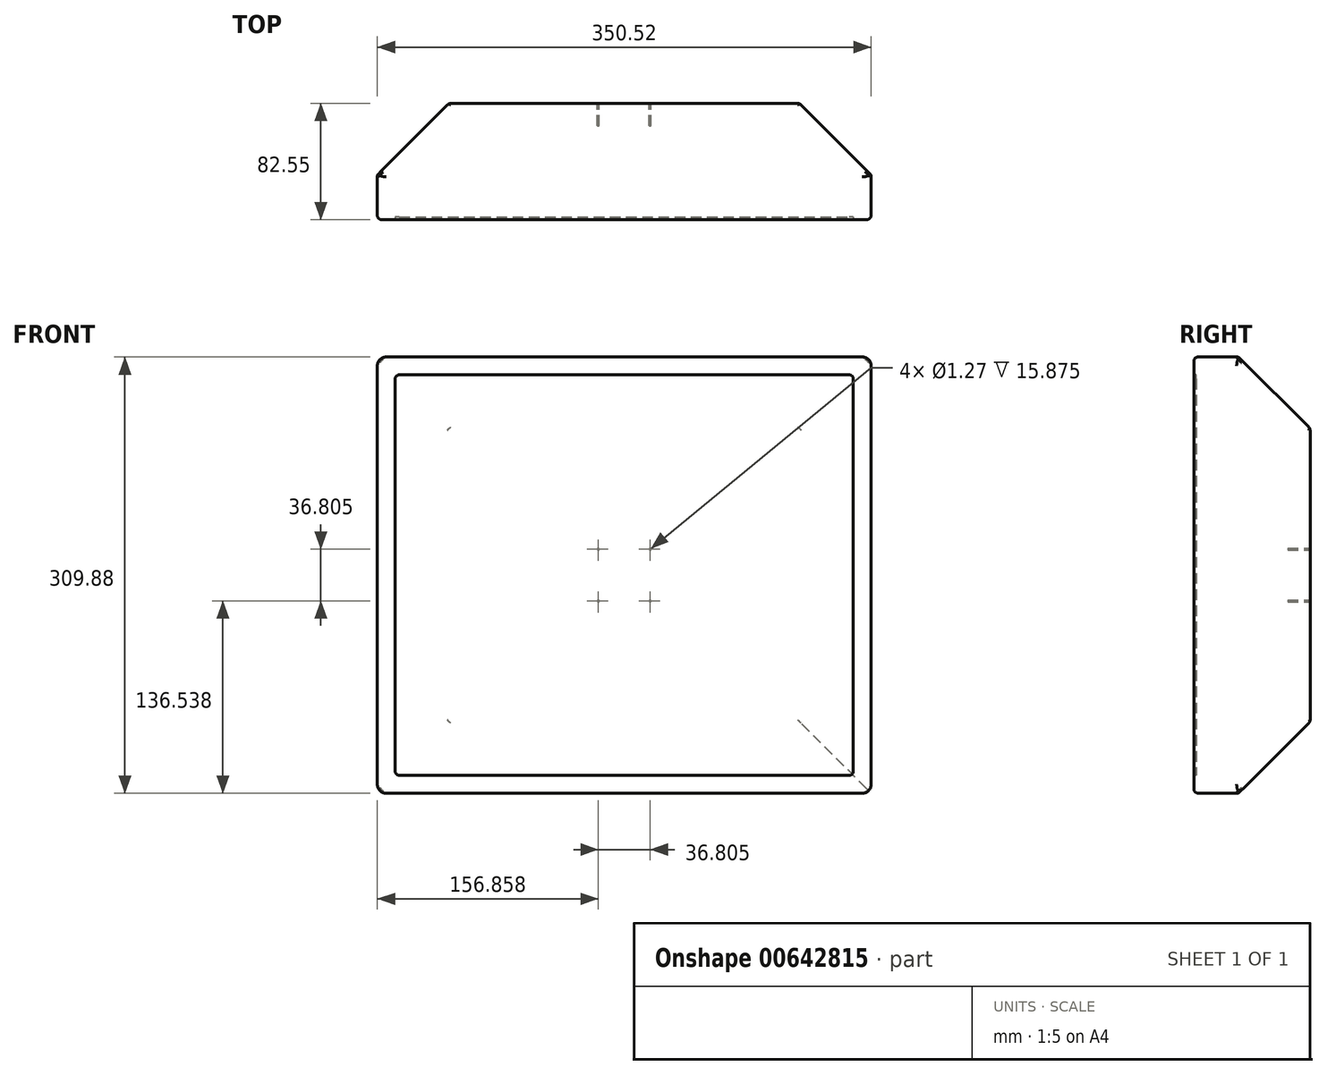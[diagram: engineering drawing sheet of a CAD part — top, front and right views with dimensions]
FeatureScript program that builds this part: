
annotation { "Feature Type Name" : "Feature", "Feature Type Description" : "" }
export const myFeature = defineFeature(function(context is Context, id is Id, definition is map)
    precondition{}
    {
        {
            var Q0;
            Q0=qCreatedBy(makeId("Front.planeOp"),FACE);
            var sketch = newSketch(context, id + "F0", { "sketchPlane" : qUnion([Q0])});
            skLineSegment(sketch, "E0.bottom", {"start": v(175.26, 154.94) * mm, "end": v(-175.26, 154.94) * mm});
            skLineSegment(sketch, "E0.top", {"start": v(175.26, -154.94) * mm, "end": v(-175.26, -154.94) * mm});
            skLineSegment(sketch, "E0.left", {"start": v(175.26, 154.94) * mm, "end": v(175.26, -154.94) * mm});
            skLineSegment(sketch, "E0.right", {"start": v(-175.26, 154.94) * mm, "end": v(-175.26, -154.94) * mm});
            skPoint(sketch, "E0.middle", {"position": v(0, 0) * mm});
            skSolve(sketch);
        }
        {
            var Q0;
            Q0 = qSketchRegion(id + "F0", true);
            extrude(context, id + "F1", {"entities" : qUnion([Q0]), "oppositeDirection" : true, "depth" : 25.4 * mm, "offsetDistance" : 25.4 * mm});
        }
        {
            var Q0;
            Q0=makeQuery(id+"F1.opExtrude","CAP_FACE",FACE,{"disambiguationData":[OSD([sQuery(id+"F0.wireOp",EDGE,"E0.bottom"),sQuery(id+"F0.wireOp",EDGE,"E0.top"),sQuery(id+"F0.wireOp",EDGE,"E0.left"),sQuery(id+"F0.wireOp",EDGE,"E0.right")])],"isStart":false});
            var sketch = newSketch(context, id + "F2", { "sketchPlane" : qUnion([Q0])});
            skLineSegment(sketch, "E1.bottom", {"start": v(175.26, 154.94) * mm, "end": v(-175.26, 154.94) * mm});
            skLineSegment(sketch, "E1.top", {"start": v(175.26, -154.94) * mm, "end": v(-175.26, -154.94) * mm});
            skLineSegment(sketch, "E1.left", {"start": v(175.26, 154.94) * mm, "end": v(175.26, -154.94) * mm});
            skLineSegment(sketch, "E1.right", {"start": v(-175.26, 154.94) * mm, "end": v(-175.26, -154.94) * mm});
            skSolve(sketch);
        }
        {
            var Q0;
            Q0 = qSketchRegion(id + "F2", true);
            extrude(context, id + "F3", {"entities" : qUnion([Q0]), "operationType" : NewBodyOperationType.ADD, "depth" : 57.15 * mm, "offsetDistance" : 25.4 * mm});
        }
        {
            var Q0;
            Q0=makeQuery(id+"F3.opExtrude","CAP_EDGE",EDGE,{"disambiguationData":[OSD([sQuery(id+"F2.wireOp",EDGE,"E1.bottom")])],"isStart":false});
            var Q1;
            Q1=makeQuery(id+"F3.opExtrude","CAP_EDGE",EDGE,{"disambiguationData":[OSD([sQuery(id+"F2.wireOp",EDGE,"E1.right")])],"isStart":false});
            var Q2;
            Q2=makeQuery(id+"F3.opExtrude","CAP_EDGE",EDGE,{"disambiguationData":[OSD([sQuery(id+"F2.wireOp",EDGE,"E1.top")])],"isStart":false});
            var Q3;
            Q3=makeQuery(id+"F3.opExtrude","CAP_EDGE",EDGE,{"disambiguationData":[OSD([sQuery(id+"F2.wireOp",EDGE,"E1.left")])],"isStart":false});
            chamfer(context, id + "F4", {"entities" : qUnion([Q0, Q1, Q2, Q3]), "chamferType" : ChamferType.TWO_OFFSETS, "width1" : 50.8 * mm, "oppositeDirection" : false, "width2" : 50.8 * mm, "tangentPropagation" : true});
        }
        {
            var Q0;
            Q0=makeQuery(id+"F1.opExtrude","CAP_FACE",FACE,{"disambiguationData":[OSD([sQuery(id+"F0.wireOp",EDGE,"E0.bottom"),sQuery(id+"F0.wireOp",EDGE,"E0.top"),sQuery(id+"F0.wireOp",EDGE,"E0.left"),sQuery(id+"F0.wireOp",EDGE,"E0.right")])],"isStart":true});
            var sketch = newSketch(context, id + "F5", { "sketchPlane" : qUnion([Q0])});
            skLineSegment(sketch, "E2.bottom", {"start": v(-162.56, 142.24) * mm, "end": v(162.56, 142.24) * mm});
            skLineSegment(sketch, "E2.top", {"start": v(-162.56, -142.24) * mm, "end": v(162.56, -142.24) * mm});
            skLineSegment(sketch, "E2.left", {"start": v(-162.56, 142.24) * mm, "end": v(-162.56, -142.24) * mm});
            skLineSegment(sketch, "E2.right", {"start": v(162.56, 142.24) * mm, "end": v(162.56, -142.24) * mm});
            skSolve(sketch);
        }
        {
            var Q0;
            Q0 = qSketchRegion(id + "F5", true);
            extrude(context, id + "F6", {"entities" : qUnion([Q0]), "operationType" : NewBodyOperationType.REMOVE, "oppositeDirection" : true, "depth" : 1.9 * mm, "offsetDistance" : 25.4 * mm});
        }
        {
            var Q0;
            Q0=makeQuery(id+"F6.boolean.opBoolean","COPY",EDGE,{"derivedFrom":makeQuery(id+"F6.opExtrude","SWEPT_EDGE",EDGE,{"disambiguationData":[OSD([sQuery(id+"F5.wireOp",EDGE,"E2.bottom"),sQuery(id+"F5.wireOp",EDGE,"E2.left")])]})});
            var Q1;
            Q1=makeQuery(id+"F6.boolean.opBoolean","COPY",EDGE,{"derivedFrom":makeQuery(id+"F6.opExtrude","SWEPT_EDGE",EDGE,{"disambiguationData":[OSD([sQuery(id+"F5.wireOp",EDGE,"E2.top"),sQuery(id+"F5.wireOp",EDGE,"E2.left")])]})});
            var Q2;
            Q2=makeQuery(id+"F6.boolean.opBoolean","COPY",EDGE,{"derivedFrom":makeQuery(id+"F6.opExtrude","SWEPT_EDGE",EDGE,{"disambiguationData":[OSD([sQuery(id+"F5.wireOp",EDGE,"E2.top"),sQuery(id+"F5.wireOp",EDGE,"E2.right")])]})});
            var Q3;
            Q3=makeQuery(id+"F6.boolean.opBoolean","COPY",EDGE,{"derivedFrom":makeQuery(id+"F6.opExtrude","SWEPT_EDGE",EDGE,{"disambiguationData":[OSD([sQuery(id+"F5.wireOp",EDGE,"E2.bottom"),sQuery(id+"F5.wireOp",EDGE,"E2.right")])]})});
            fillet(context, id + "F7", {"entities" : qUnion([Q0, Q1, Q2, Q3]), "radius" : 2.87 * mm, "tangentPropagation" : true, "allowEdgeOverflow" : false});
        }
        {
            var Q0;
            Q0=makeQuery(id+"F3.boolean.opBoolean","MERGE",EDGE,{"derivedFrom":[makeQuery(id+"F1.opExtrude","SWEPT_EDGE",EDGE,{"disambiguationData":[OSD([sQuery(id+"F0.wireOp",EDGE,"E0.bottom"),sQuery(id+"F0.wireOp",EDGE,"E0.left")])]}),makeQuery(id+"F3.opExtrude","SWEPT_EDGE",EDGE,{"disambiguationData":[OSD([sQuery(id+"F2.wireOp",EDGE,"E1.bottom"),sQuery(id+"F2.wireOp",EDGE,"E1.right")])]})]});
            var Q1;
            Q1=makeQuery(id+"F3.boolean.opBoolean","MERGE",EDGE,{"derivedFrom":[makeQuery(id+"F1.opExtrude","SWEPT_EDGE",EDGE,{"disambiguationData":[OSD([sQuery(id+"F0.wireOp",EDGE,"E0.bottom"),sQuery(id+"F0.wireOp",EDGE,"E0.right")])]}),makeQuery(id+"F3.opExtrude","SWEPT_EDGE",EDGE,{"disambiguationData":[OSD([sQuery(id+"F2.wireOp",EDGE,"E1.bottom"),sQuery(id+"F2.wireOp",EDGE,"E1.left")])]})]});
            var Q2;
            Q2=makeQuery(id+"F3.boolean.opBoolean","MERGE",EDGE,{"derivedFrom":[makeQuery(id+"F1.opExtrude","SWEPT_EDGE",EDGE,{"disambiguationData":[OSD([sQuery(id+"F0.wireOp",EDGE,"E0.top"),sQuery(id+"F0.wireOp",EDGE,"E0.left")])]}),makeQuery(id+"F3.opExtrude","SWEPT_EDGE",EDGE,{"disambiguationData":[OSD([sQuery(id+"F2.wireOp",EDGE,"E1.top"),sQuery(id+"F2.wireOp",EDGE,"E1.right")])]})]});
            var Q3;
            Q3=makeQuery(id+"F3.boolean.opBoolean","MERGE",EDGE,{"derivedFrom":[makeQuery(id+"F1.opExtrude","SWEPT_EDGE",EDGE,{"disambiguationData":[OSD([sQuery(id+"F0.wireOp",EDGE,"E0.top"),sQuery(id+"F0.wireOp",EDGE,"E0.right")])]}),makeQuery(id+"F3.opExtrude","SWEPT_EDGE",EDGE,{"disambiguationData":[OSD([sQuery(id+"F2.wireOp",EDGE,"E1.top"),sQuery(id+"F2.wireOp",EDGE,"E1.left")])]})]});
            fillet(context, id + "F8", {"entities" : qUnion([Q0, Q1, Q2, Q3]), "radius" : 6.35 * mm, "tangentPropagation" : true, "allowEdgeOverflow" : false});
        }
        {
            var Q0;
            Q0=makeQuery(id+"F1.opExtrude","CAP_EDGE",EDGE,{"disambiguationData":[OSD([sQuery(id+"F0.wireOp",EDGE,"E0.bottom")])],"isStart":true});
            var Q1;
            {var subQ0=sQuery(id+"F2.wireOp",EDGE,"E1.bottom");Q1=makeQuery(id+"F4.opChamfer","BLEND_EDGE",EDGE,{"blendedFrom":[makeQuery(id+"F3.opExtrude","CAP_EDGE",EDGE,{"disambiguationData":[OSD([subQ0])],"isStart":false}),makeQuery(id+"F3.boolean.opBoolean","MERGE",FACE,{"derivedFrom":[makeQuery(id+"F1.opExtrude","SWEPT_FACE",FACE,{"disambiguationData":[OSD([sQuery(id+"F0.wireOp",EDGE,"E0.bottom")])]}),makeQuery(id+"F3.opExtrude","SWEPT_FACE",FACE,{"disambiguationData":[OSD([subQ0])]})]})],"blendedInto":[makeQuery(id+"F3.boolean.opBoolean","MERGE",FACE,{"derivedFrom":[makeQuery(id+"F1.opExtrude","SWEPT_FACE",FACE,{"disambiguationData":[OSD([sQuery(id+"F0.wireOp",EDGE,"E0.bottom")])]}),makeQuery(id+"F3.opExtrude","SWEPT_FACE",FACE,{"disambiguationData":[OSD([subQ0])]})]})]});}
            var Q2;
            {var subQ0=sQuery(id+"F2.wireOp",EDGE,"E1.right");Q2=makeQuery(id+"F8.opFillet","BLEND_EDGE",EDGE,{"blendedFrom":[makeQuery(id+"F3.boolean.opBoolean","MERGE",EDGE,{"derivedFrom":[makeQuery(id+"F1.opExtrude","SWEPT_EDGE",EDGE,{"disambiguationData":[OSD([sQuery(id+"F0.wireOp",EDGE,"E0.bottom"),sQuery(id+"F0.wireOp",EDGE,"E0.left")])]}),makeQuery(id+"F3.opExtrude","SWEPT_EDGE",EDGE,{"disambiguationData":[OSD([sQuery(id+"F2.wireOp",EDGE,"E1.bottom"),subQ0])]})]}),makeQuery(id+"F4.opChamfer","BLEND_FACE",FACE,{"disambiguationData":[OSD([subQ0])]})],"blendedInto":[makeQuery(id+"F4.opChamfer","BLEND_FACE",FACE,{"disambiguationData":[OSD([subQ0])]})]});}
            var Q3;
            {var subQ0=sQuery(id+"F2.wireOp",EDGE,"E1.top");Q3=makeQuery(id+"F4.opChamfer","BLEND_EDGE",EDGE,{"blendedFrom":[makeQuery(id+"F3.opExtrude","CAP_EDGE",EDGE,{"disambiguationData":[OSD([subQ0])],"isStart":false}),makeQuery(id+"F3.boolean.opBoolean","MERGE",FACE,{"derivedFrom":[makeQuery(id+"F1.opExtrude","SWEPT_FACE",FACE,{"disambiguationData":[OSD([sQuery(id+"F0.wireOp",EDGE,"E0.top")])]}),makeQuery(id+"F3.opExtrude","SWEPT_FACE",FACE,{"disambiguationData":[OSD([subQ0])]})]})],"blendedInto":[makeQuery(id+"F3.boolean.opBoolean","MERGE",FACE,{"derivedFrom":[makeQuery(id+"F1.opExtrude","SWEPT_FACE",FACE,{"disambiguationData":[OSD([sQuery(id+"F0.wireOp",EDGE,"E0.top")])]}),makeQuery(id+"F3.opExtrude","SWEPT_FACE",FACE,{"disambiguationData":[OSD([subQ0])]})]})]});}
            var Q4;
            {var subQ0=sQuery(id+"F2.wireOp",EDGE,"E1.left");Q4=makeQuery(id+"F4.opChamfer","BLEND_EDGE",EDGE,{"blendedFrom":[makeQuery(id+"F3.opExtrude","CAP_EDGE",EDGE,{"disambiguationData":[OSD([subQ0])],"isStart":false}),makeQuery(id+"F3.boolean.opBoolean","MERGE",FACE,{"derivedFrom":[makeQuery(id+"F1.opExtrude","SWEPT_FACE",FACE,{"disambiguationData":[OSD([sQuery(id+"F0.wireOp",EDGE,"E0.right")])]}),makeQuery(id+"F3.opExtrude","SWEPT_FACE",FACE,{"disambiguationData":[OSD([subQ0])]})]})],"blendedInto":[makeQuery(id+"F3.boolean.opBoolean","MERGE",FACE,{"derivedFrom":[makeQuery(id+"F1.opExtrude","SWEPT_FACE",FACE,{"disambiguationData":[OSD([sQuery(id+"F0.wireOp",EDGE,"E0.right")])]}),makeQuery(id+"F3.opExtrude","SWEPT_FACE",FACE,{"disambiguationData":[OSD([subQ0])]})]})]});}
            var Q5;
            Q5=makeQuery(id+"F4.opChamfer","BLEND_EDGE",EDGE,{"blendedFrom":[makeQuery(id+"F3.opExtrude","CAP_EDGE",EDGE,{"disambiguationData":[OSD([sQuery(id+"F2.wireOp",EDGE,"E1.top")])],"isStart":false}),makeQuery(id+"F3.opExtrude","CAP_EDGE",EDGE,{"disambiguationData":[OSD([sQuery(id+"F2.wireOp",EDGE,"E1.left")])],"isStart":false})],"blendedInto":[]});
            var Q6;
            {var subQ0=sQuery(id+"F2.wireOp",EDGE,"E1.left");Q6=makeQuery(id+"F4.opChamfer","BLEND_EDGE",EDGE,{"blendedFrom":[makeQuery(id+"F3.opExtrude","CAP_EDGE",EDGE,{"disambiguationData":[OSD([subQ0])],"isStart":false}),makeQuery(id+"F3.opExtrude","CAP_FACE",FACE,{"disambiguationData":[OSD([sQuery(id+"F2.wireOp",EDGE,"E1.bottom"),sQuery(id+"F2.wireOp",EDGE,"E1.top"),subQ0,sQuery(id+"F2.wireOp",EDGE,"E1.right")])],"isStart":false})],"blendedInto":[makeQuery(id+"F3.opExtrude","CAP_FACE",FACE,{"disambiguationData":[OSD([sQuery(id+"F2.wireOp",EDGE,"E1.bottom"),sQuery(id+"F2.wireOp",EDGE,"E1.top"),subQ0,sQuery(id+"F2.wireOp",EDGE,"E1.right")])],"isStart":false})]});}
            var Q7;
            {var subQ0=sQuery(id+"F2.wireOp",EDGE,"E1.top");Q7=makeQuery(id+"F4.opChamfer","BLEND_EDGE",EDGE,{"blendedFrom":[makeQuery(id+"F3.opExtrude","CAP_EDGE",EDGE,{"disambiguationData":[OSD([subQ0])],"isStart":false}),makeQuery(id+"F3.opExtrude","CAP_FACE",FACE,{"disambiguationData":[OSD([sQuery(id+"F2.wireOp",EDGE,"E1.bottom"),subQ0,sQuery(id+"F2.wireOp",EDGE,"E1.left"),sQuery(id+"F2.wireOp",EDGE,"E1.right")])],"isStart":false})],"blendedInto":[makeQuery(id+"F3.opExtrude","CAP_FACE",FACE,{"disambiguationData":[OSD([sQuery(id+"F2.wireOp",EDGE,"E1.bottom"),subQ0,sQuery(id+"F2.wireOp",EDGE,"E1.left"),sQuery(id+"F2.wireOp",EDGE,"E1.right")])],"isStart":false})]});}
            var Q8;
            {var subQ0=sQuery(id+"F2.wireOp",EDGE,"E1.bottom");Q8=makeQuery(id+"F4.opChamfer","BLEND_EDGE",EDGE,{"blendedFrom":[makeQuery(id+"F3.opExtrude","CAP_EDGE",EDGE,{"disambiguationData":[OSD([subQ0])],"isStart":false}),makeQuery(id+"F3.opExtrude","CAP_FACE",FACE,{"disambiguationData":[OSD([subQ0,sQuery(id+"F2.wireOp",EDGE,"E1.top"),sQuery(id+"F2.wireOp",EDGE,"E1.left"),sQuery(id+"F2.wireOp",EDGE,"E1.right")])],"isStart":false})],"blendedInto":[makeQuery(id+"F3.opExtrude","CAP_FACE",FACE,{"disambiguationData":[OSD([subQ0,sQuery(id+"F2.wireOp",EDGE,"E1.top"),sQuery(id+"F2.wireOp",EDGE,"E1.left"),sQuery(id+"F2.wireOp",EDGE,"E1.right")])],"isStart":false})]});}
            var Q9;
            Q9=makeQuery(id+"F4.opChamfer","BLEND_EDGE",EDGE,{"blendedFrom":[makeQuery(id+"F3.opExtrude","CAP_EDGE",EDGE,{"disambiguationData":[OSD([sQuery(id+"F2.wireOp",EDGE,"E1.bottom")])],"isStart":false}),makeQuery(id+"F3.opExtrude","CAP_EDGE",EDGE,{"disambiguationData":[OSD([sQuery(id+"F2.wireOp",EDGE,"E1.left")])],"isStart":false})],"blendedInto":[]});
            var Q10;
            Q10=makeQuery(id+"F4.opChamfer","BLEND_EDGE",EDGE,{"blendedFrom":[makeQuery(id+"F3.opExtrude","CAP_EDGE",EDGE,{"disambiguationData":[OSD([sQuery(id+"F2.wireOp",EDGE,"E1.bottom")])],"isStart":false}),makeQuery(id+"F3.opExtrude","CAP_EDGE",EDGE,{"disambiguationData":[OSD([sQuery(id+"F2.wireOp",EDGE,"E1.right")])],"isStart":false})],"blendedInto":[]});
            var Q11;
            {var subQ0=sQuery(id+"F2.wireOp",EDGE,"E1.right");Q11=makeQuery(id+"F4.opChamfer","BLEND_EDGE",EDGE,{"blendedFrom":[makeQuery(id+"F3.opExtrude","CAP_EDGE",EDGE,{"disambiguationData":[OSD([subQ0])],"isStart":false}),makeQuery(id+"F3.opExtrude","CAP_FACE",FACE,{"disambiguationData":[OSD([sQuery(id+"F2.wireOp",EDGE,"E1.bottom"),sQuery(id+"F2.wireOp",EDGE,"E1.top"),sQuery(id+"F2.wireOp",EDGE,"E1.left"),subQ0])],"isStart":false})],"blendedInto":[makeQuery(id+"F3.opExtrude","CAP_FACE",FACE,{"disambiguationData":[OSD([sQuery(id+"F2.wireOp",EDGE,"E1.bottom"),sQuery(id+"F2.wireOp",EDGE,"E1.top"),sQuery(id+"F2.wireOp",EDGE,"E1.left"),subQ0])],"isStart":false})]});}
            fillet(context, id + "F9", {"entities" : qUnion([Q0, Q1, Q2, Q3, Q4, Q5, Q6, Q7, Q8, Q9, Q10, Q11]), "radius" : 3.17 * mm, "tangentPropagation" : true, "allowEdgeOverflow" : false});
        }
        {
            var Q0;
            Q0=makeQuery(id+"F3.opExtrude","CAP_FACE",FACE,{"disambiguationData":[OSD([sQuery(id+"F2.wireOp",EDGE,"E1.bottom"),sQuery(id+"F2.wireOp",EDGE,"E1.top"),sQuery(id+"F2.wireOp",EDGE,"E1.left"),sQuery(id+"F2.wireOp",EDGE,"E1.right")])],"isStart":false});
            var sketch = newSketch(context, id + "F10", { "sketchPlane" : qUnion([Q0])});
            skCircle(sketch, "E3", {"center": v(-18.4, 18.4) * mm, "radius": 0.64 * mm});
            skCircle(sketch, "E4", {"center": v(18.4, 18.4) * mm, "radius": 0.64 * mm});
            skCircle(sketch, "E5", {"center": v(-18.4, -18.4) * mm, "radius": 0.64 * mm});
            skCircle(sketch, "E6", {"center": v(18.4, -18.4) * mm, "radius": 0.64 * mm});
            skSolve(sketch);
        }
        {
            var Q0;
            Q0 = qSketchRegion(id + "F10", true);
            extrude(context, id + "F11", {"entities" : qUnion([Q0]), "operationType" : NewBodyOperationType.REMOVE, "oppositeDirection" : true, "depth" : 15.88 * mm, "offsetDistance" : 25.4 * mm});
        }
    });
